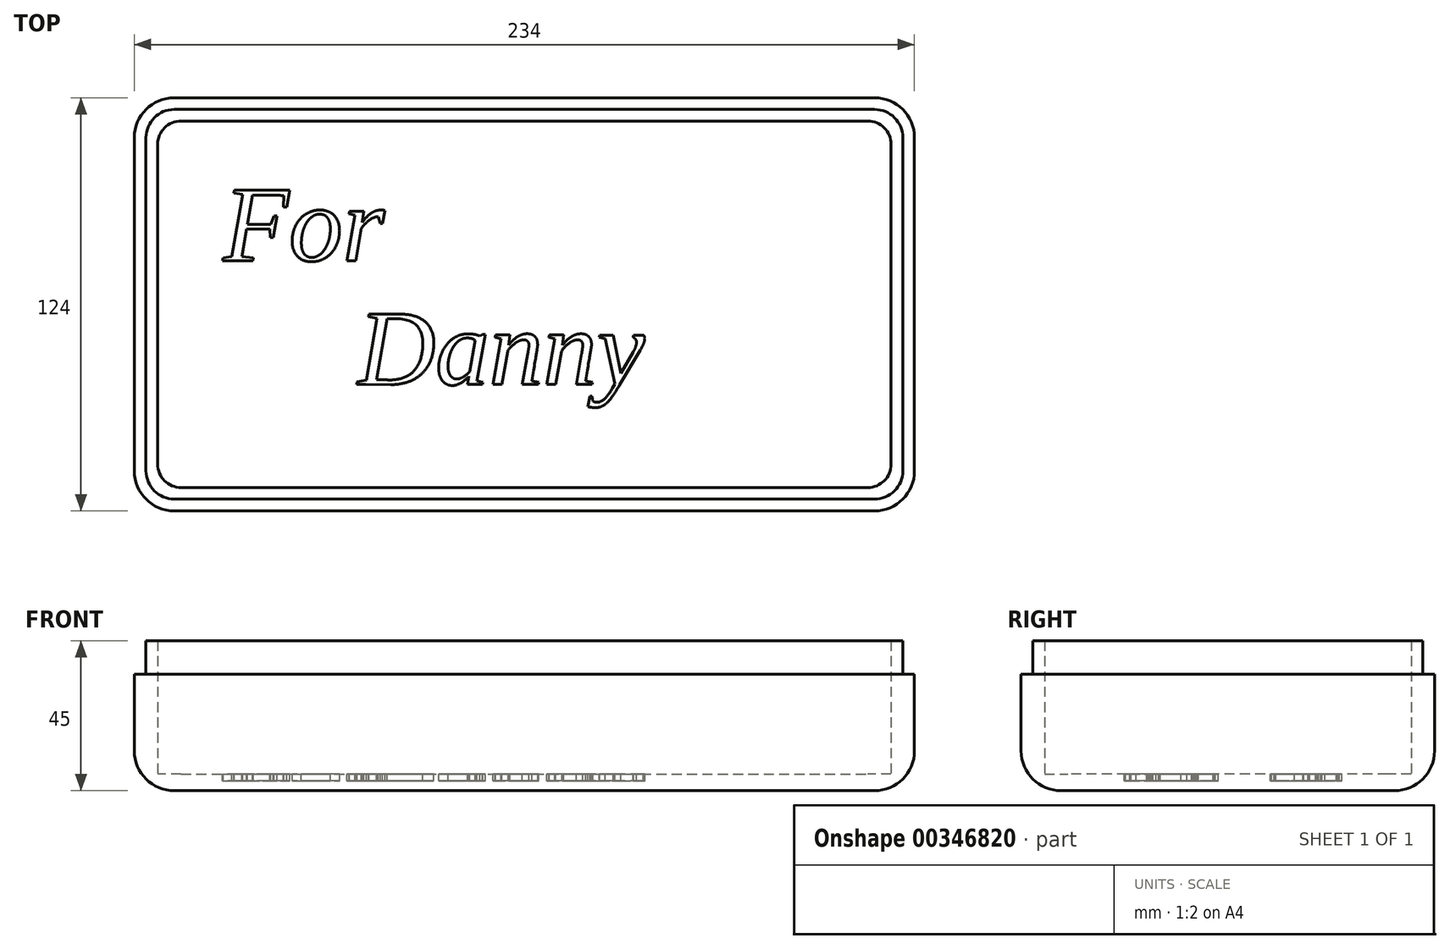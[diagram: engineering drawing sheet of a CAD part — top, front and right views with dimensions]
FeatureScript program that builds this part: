
annotation { "Feature Type Name" : "Feature", "Feature Type Description" : "" }
export const myFeature = defineFeature(function(context is Context, id is Id, definition is map)
    precondition{}
    {
        {
            var Q0;
            Q0=qCreatedBy(makeId("Top.planeOp"),FACE);
            var sketch = newSketch(context, id + "F0", { "sketchPlane" : qUnion([Q0])});
            skLineSegment(sketch, "E0.bottom", {"start": v(-110, 55) * mm, "end": v(110, 55) * mm});
            skLineSegment(sketch, "E0.top", {"start": v(-110, -55) * mm, "end": v(110, -55) * mm});
            skLineSegment(sketch, "E0.left", {"start": v(-110, 55) * mm, "end": v(-110, -55) * mm});
            skLineSegment(sketch, "E0.right", {"start": v(110, 55) * mm, "end": v(110, -55) * mm});
            skPoint(sketch, "E0.middle", {"position": v(0, 0) * mm});
            skLineSegment(sketch, "E1.bottom", {"start": v(-117, 62) * mm, "end": v(117, 62) * mm});
            skLineSegment(sketch, "E1.top", {"start": v(-117, -62) * mm, "end": v(117, -62) * mm});
            skLineSegment(sketch, "E1.left", {"start": v(-117, 62) * mm, "end": v(-117, -62) * mm});
            skLineSegment(sketch, "E1.right", {"start": v(117, 62) * mm, "end": v(117, -62) * mm});
            skSolve(sketch);
        }
        {
            var Q0;
            Q0=makeQuery(id+"F0.imprint","IMPRINT",FACE,{"disambiguationData":[TD([[makeQuery(id+"F0.imprint","IMPRINT",EDGE,{"derivedFrom":sQuery(id+"F0.wireOp",EDGE,"E0.bottom")}),1.0]])]});
            extrude(context, id + "F1", {"entities" : qUnion([Q0]), "depth" : 40 * mm});
        }
        {
            var Q0;
            Q0=makeQuery(id+"F1.opExtrude","CAP_FACE",FACE,{"disambiguationData":[OSD([sQuery(id+"F0.wireOp",EDGE,"E0.bottom"),sQuery(id+"F0.wireOp",EDGE,"E0.top"),sQuery(id+"F0.wireOp",EDGE,"E0.left"),sQuery(id+"F0.wireOp",EDGE,"E0.right"),sQuery(id+"F0.wireOp",EDGE,"E1.bottom"),sQuery(id+"F0.wireOp",EDGE,"E1.top"),sQuery(id+"F0.wireOp",EDGE,"E1.left"),sQuery(id+"F0.wireOp",EDGE,"E1.right")])],"isStart":true});
            var sketch = newSketch(context, id + "F2", { "sketchPlane" : qUnion([Q0])});
            skLineSegment(sketch, "E2.bottom", {"start": v(-117, 62) * mm, "end": v(117, 62) * mm});
            skLineSegment(sketch, "E2.top", {"start": v(-117, -62) * mm, "end": v(117, -62) * mm});
            skLineSegment(sketch, "E2.left", {"start": v(-117, 62) * mm, "end": v(-117, -62) * mm});
            skLineSegment(sketch, "E2.right", {"start": v(117, 62) * mm, "end": v(117, -62) * mm});
            skSolve(sketch);
        }
        {
            var Q0;
            Q0 = qSketchRegion(id + "F2", true);
            extrude(context, id + "F3", {"entities" : qUnion([Q0]), "operationType" : NewBodyOperationType.ADD, "depth" : 5 * mm});
        }
        {
            var Q0;
            Q0=makeQuery(id+"F3.boolean.opBoolean","MERGE",EDGE,{"derivedFrom":[makeQuery(id+"F1.opExtrude","SWEPT_EDGE",EDGE,{"disambiguationData":[OSD([sQuery(id+"F0.wireOp",EDGE,"E1.top"),sQuery(id+"F0.wireOp",EDGE,"E1.left")])]}),makeQuery(id+"F3.opExtrude","SWEPT_EDGE",EDGE,{"disambiguationData":[OSD([sQuery(id+"F2.wireOp",EDGE,"E2.bottom"),sQuery(id+"F2.wireOp",EDGE,"E2.left")])]})]});
            var Q1;
            Q1=makeQuery(id+"F3.boolean.opBoolean","MERGE",EDGE,{"derivedFrom":[makeQuery(id+"F1.opExtrude","SWEPT_EDGE",EDGE,{"disambiguationData":[OSD([sQuery(id+"F0.wireOp",EDGE,"E1.top"),sQuery(id+"F0.wireOp",EDGE,"E1.right")])]}),makeQuery(id+"F3.opExtrude","SWEPT_EDGE",EDGE,{"disambiguationData":[OSD([sQuery(id+"F2.wireOp",EDGE,"E2.bottom"),sQuery(id+"F2.wireOp",EDGE,"E2.right")])]})]});
            var Q2;
            Q2=makeQuery(id+"F3.boolean.opBoolean","MERGE",EDGE,{"derivedFrom":[makeQuery(id+"F1.opExtrude","SWEPT_EDGE",EDGE,{"disambiguationData":[OSD([sQuery(id+"F0.wireOp",EDGE,"E1.bottom"),sQuery(id+"F0.wireOp",EDGE,"E1.right")])]}),makeQuery(id+"F3.opExtrude","SWEPT_EDGE",EDGE,{"disambiguationData":[OSD([sQuery(id+"F2.wireOp",EDGE,"E2.top"),sQuery(id+"F2.wireOp",EDGE,"E2.right")])]})]});
            var Q3;
            Q3=makeQuery(id+"F3.boolean.opBoolean","MERGE",EDGE,{"derivedFrom":[makeQuery(id+"F1.opExtrude","SWEPT_EDGE",EDGE,{"disambiguationData":[OSD([sQuery(id+"F0.wireOp",EDGE,"E1.bottom"),sQuery(id+"F0.wireOp",EDGE,"E1.left")])]}),makeQuery(id+"F3.opExtrude","SWEPT_EDGE",EDGE,{"disambiguationData":[OSD([sQuery(id+"F2.wireOp",EDGE,"E2.top"),sQuery(id+"F2.wireOp",EDGE,"E2.left")])]})]});
            var Q4;
            Q4=makeQuery(id+"F3.opExtrude","CAP_EDGE",EDGE,{"disambiguationData":[OSD([sQuery(id+"F2.wireOp",EDGE,"E2.bottom")])],"isStart":false});
            var Q5;
            Q5=makeQuery(id+"F3.opExtrude","CAP_EDGE",EDGE,{"disambiguationData":[OSD([sQuery(id+"F2.wireOp",EDGE,"E2.left")])],"isStart":false});
            var Q6;
            Q6=makeQuery(id+"F3.opExtrude","CAP_EDGE",EDGE,{"disambiguationData":[OSD([sQuery(id+"F2.wireOp",EDGE,"E2.right")])],"isStart":false});
            var Q7;
            Q7=makeQuery(id+"F3.opExtrude","CAP_EDGE",EDGE,{"disambiguationData":[OSD([sQuery(id+"F2.wireOp",EDGE,"E2.top")])],"isStart":false});
            fillet(context, id + "F4", {"entities" : qUnion([Q0, Q1, Q2, Q3, Q4, Q5, Q6, Q7]), "radius" : 12 * mm, "tangentPropagation" : true, "allowEdgeOverflow" : false});
        }
        {
            var Q0;
            Q0=makeQuery(id+"F1.opExtrude","SWEPT_EDGE",EDGE,{"disambiguationData":[OSD([sQuery(id+"F0.wireOp",EDGE,"E0.bottom"),sQuery(id+"F0.wireOp",EDGE,"E0.left")])]});
            var Q1;
            Q1=makeQuery(id+"F1.opExtrude","SWEPT_EDGE",EDGE,{"disambiguationData":[OSD([sQuery(id+"F0.wireOp",EDGE,"E0.bottom"),sQuery(id+"F0.wireOp",EDGE,"E0.right")])]});
            var Q2;
            Q2=makeQuery(id+"F1.opExtrude","SWEPT_EDGE",EDGE,{"disambiguationData":[OSD([sQuery(id+"F0.wireOp",EDGE,"E0.top"),sQuery(id+"F0.wireOp",EDGE,"E0.right")])]});
            var Q3;
            Q3=makeQuery(id+"F1.opExtrude","SWEPT_EDGE",EDGE,{"disambiguationData":[OSD([sQuery(id+"F0.wireOp",EDGE,"E0.top"),sQuery(id+"F0.wireOp",EDGE,"E0.left")])]});
            var Q4;
            Q4=makeQuery(id+"F1.opExtrude","CAP_EDGE",EDGE,{"disambiguationData":[OSD([sQuery(id+"F0.wireOp",EDGE,"E0.bottom")])],"isStart":true});
            var Q5;
            Q5=makeQuery(id+"F1.opExtrude","CAP_EDGE",EDGE,{"disambiguationData":[OSD([sQuery(id+"F0.wireOp",EDGE,"E0.left")])],"isStart":true});
            var Q6;
            Q6=makeQuery(id+"F1.opExtrude","CAP_EDGE",EDGE,{"disambiguationData":[OSD([sQuery(id+"F0.wireOp",EDGE,"E0.top")])],"isStart":true});
            var Q7;
            Q7=makeQuery(id+"F1.opExtrude","CAP_EDGE",EDGE,{"disambiguationData":[OSD([sQuery(id+"F0.wireOp",EDGE,"E0.right")])],"isStart":true});
            fillet(context, id + "F5", {"entities" : qUnion([Q0, Q1, Q2, Q3, Q4, Q5, Q6, Q7]), "radius" : 7 * mm, "tangentPropagation" : true, "allowEdgeOverflow" : false});
        }
        {
            var Q0;
            Q0=makeQuery(id+"F1.opExtrude","CAP_FACE",FACE,{"disambiguationData":[OSD([sQuery(id+"F0.wireOp",EDGE,"E0.bottom"),sQuery(id+"F0.wireOp",EDGE,"E0.top"),sQuery(id+"F0.wireOp",EDGE,"E0.left"),sQuery(id+"F0.wireOp",EDGE,"E0.right"),sQuery(id+"F0.wireOp",EDGE,"E1.bottom"),sQuery(id+"F0.wireOp",EDGE,"E1.top"),sQuery(id+"F0.wireOp",EDGE,"E1.left"),sQuery(id+"F0.wireOp",EDGE,"E1.right")])],"isStart":false});
            var sketch = newSketch(context, id + "F6", { "sketchPlane" : qUnion([Q0])});
            skLineSegment(sketch, "E3.0.0", {"start": v(-117, 50) * mm, "end": v(-117, -50) * mm});
            skArc(sketch, "E3.0.1", {"start": v(-117, -50) * mm, "mid": v(-113.49, -58.49) * mm, "end": v(-105, -62) * mm});
            skLineSegment(sketch, "E3.0.2", {"start": v(-105, -62) * mm, "end": v(105, -62) * mm});
            skArc(sketch, "E3.0.3", {"start": v(105, -62) * mm, "mid": v(113.49, -58.49) * mm, "end": v(117, -50) * mm});
            skLineSegment(sketch, "E3.0.4", {"start": v(117, -50) * mm, "end": v(117, 50) * mm});
            skArc(sketch, "E3.0.5", {"start": v(117, 50) * mm, "mid": v(113.49, 58.49) * mm, "end": v(105, 62) * mm});
            skLineSegment(sketch, "E3.0.6", {"start": v(105, 62) * mm, "end": v(-105, 62) * mm});
            skArc(sketch, "E3.0.7", {"start": v(-105, 62) * mm, "mid": v(-113.49, 58.49) * mm, "end": v(-117, 50) * mm});
            skArc(sketch, "E4.0", {"start": v(113.5, 50) * mm, "mid": v(111.01, 56.01) * mm, "end": v(105, 58.5) * mm});
            skLineSegment(sketch, "E4.1", {"start": v(113.5, -50) * mm, "end": v(113.5, 50) * mm});
            skLineSegment(sketch, "E4.2", {"start": v(105, 58.5) * mm, "end": v(-105, 58.5) * mm});
            skArc(sketch, "E4.3", {"start": v(105, -58.5) * mm, "mid": v(111.01, -56.01) * mm, "end": v(113.5, -50) * mm});
            skArc(sketch, "E4.4", {"start": v(-105, 58.5) * mm, "mid": v(-111.01, 56.01) * mm, "end": v(-113.5, 50) * mm});
            skLineSegment(sketch, "E4.5", {"start": v(-113.5, 50) * mm, "end": v(-113.5, -50) * mm});
            skArc(sketch, "E4.6", {"start": v(-113.5, -50) * mm, "mid": v(-111.01, -56.01) * mm, "end": v(-105, -58.5) * mm});
            skLineSegment(sketch, "E4.7", {"start": v(-105, -58.5) * mm, "end": v(105, -58.5) * mm});
            skSolve(sketch);
        }
        {
            var Q0;
            Q0 = qSketchRegion(id + "F6", true);
            extrude(context, id + "F7", {"entities" : qUnion([Q0]), "operationType" : NewBodyOperationType.REMOVE, "oppositeDirection" : true, "depth" : 10 * mm});
        }
        {
            var Q0;
            Q0=makeQuery(id+"F3.opExtrude","CAP_FACE",FACE,{"disambiguationData":[OSD([sQuery(id+"F2.wireOp",EDGE,"E2.bottom"),sQuery(id+"F2.wireOp",EDGE,"E2.top"),sQuery(id+"F2.wireOp",EDGE,"E2.left"),sQuery(id+"F2.wireOp",EDGE,"E2.right")])],"isStart":true});
            var sketch = newSketch(context, id + "F8", { "sketchPlane" : qUnion([Q0])});
            skText(sketch, "E5", { "text": "For\n     Danny", "fontName": "Tinos-Italic.ttf"});
            const initialGuessF8  = {"E5": [-0.09037, 0.01308, 1, 0, 0.02325]};
            skSetInitialGuess(sketch, initialGuessF8);
            skSolve(sketch);
        }
        {
            var Q0;
            Q0 = qSketchRegion(id + "F8", true);
            extrude(context, id + "F9", {"entities" : qUnion([Q0]), "operationType" : NewBodyOperationType.REMOVE, "oppositeDirection" : true, "depth" : 2 * mm});
        }
    });
